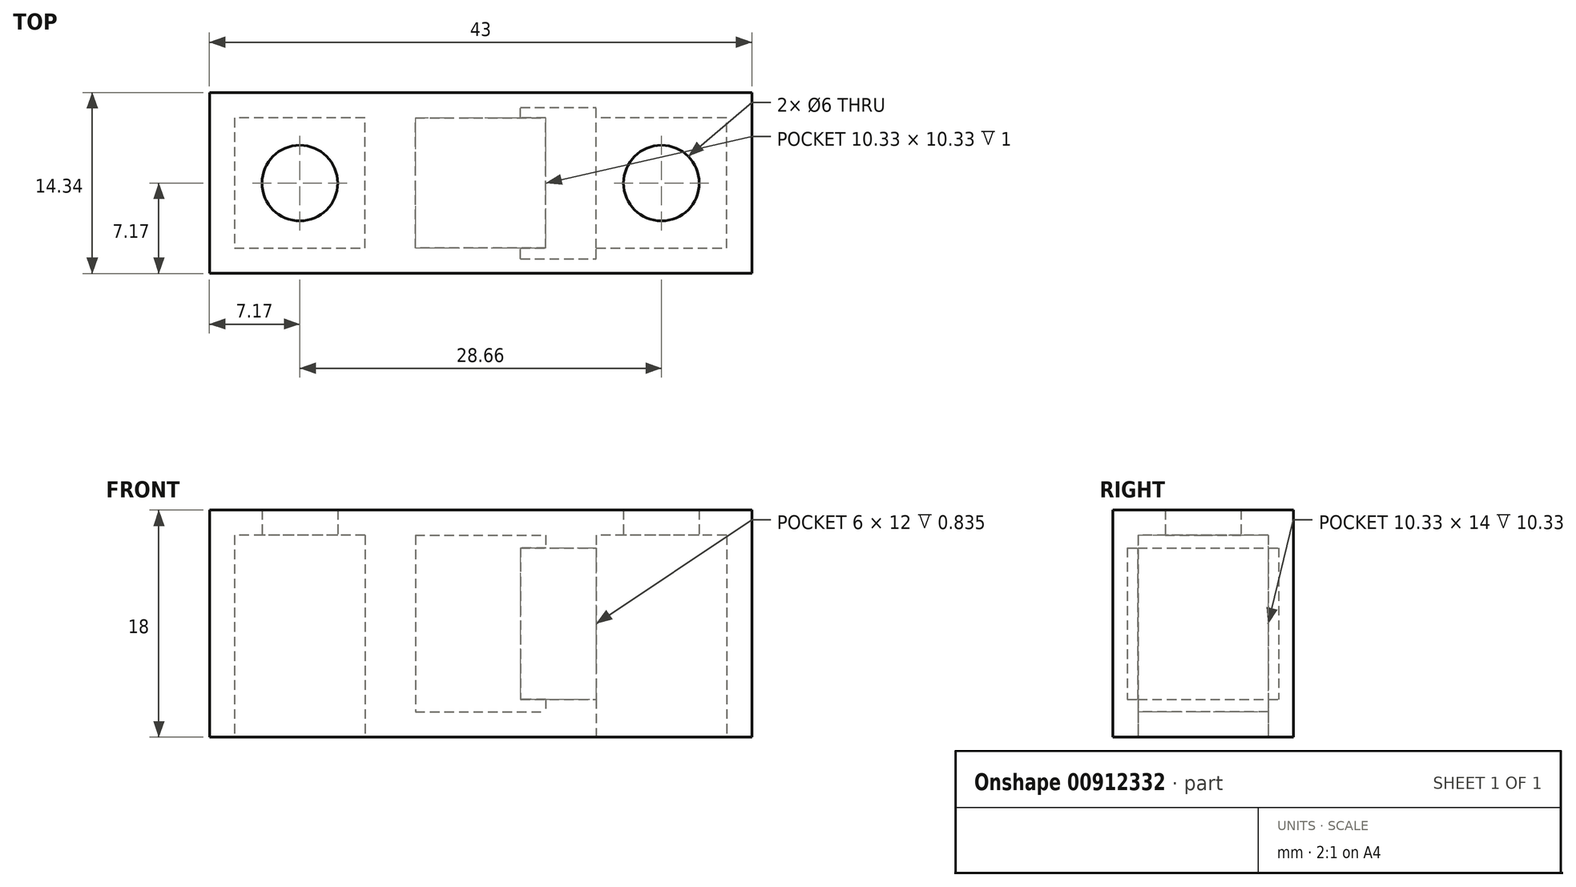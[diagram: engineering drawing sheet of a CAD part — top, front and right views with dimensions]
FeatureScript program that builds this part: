
annotation { "Feature Type Name" : "Feature", "Feature Type Description" : "" }
export const myFeature = defineFeature(function(context is Context, id is Id, definition is map)
    precondition{}
    {
        {
            var Q0;
            Q0=qCreatedBy(makeId("Top.planeOp"),FACE);
            var sketch = newSketch(context, id + "F0", { "sketchPlane" : qUnion([Q0])});
            skLineSegment(sketch, "E0.bottom", {"start": v(-3.17, 3.17) * mm, "end": v(3.16, 3.17) * mm});
            skLineSegment(sketch, "E0.top", {"start": v(-3.17, -3.17) * mm, "end": v(3.17, -3.17) * mm});
            skLineSegment(sketch, "E0.left", {"start": v(-3.17, 3.17) * mm, "end": v(-3.17, -3.17) * mm});
            skLineSegment(sketch, "E0.right", {"start": v(3.17, 3.17) * mm, "end": v(3.17, -3.17) * mm});
            skLineSegment(sketch, "E1", {"start": v(-3.17, 0) * mm, "end": v(3.17, 0) * mm, "construction": true});
            skLineSegment(sketch, "E2", {"start": v(-3.17, 3.17) * mm, "end": v(-5.17, 3.17) * mm, "construction": true});
            skLineSegment(sketch, "E3", {"start": v(-3.17, 3.17) * mm, "end": v(-3.17, 5.17) * mm, "construction": true});
            skLineSegment(sketch, "E4", {"start": v(-5.16, 5.17) * mm, "end": v(5.17, 5.17) * mm});
            skLineSegment(sketch, "E5", {"start": v(5.17, 5.17) * mm, "end": v(5.17, -5.17) * mm});
            skLineSegment(sketch, "E6", {"start": v(5.17, -5.17) * mm, "end": v(-5.16, -5.17) * mm});
            skLineSegment(sketch, "E7", {"start": v(-5.17, -5.16) * mm, "end": v(-5.17, 5.17) * mm});
            skLineSegment(sketch, "E8", {"start": v(3.17, -3.17) * mm, "end": v(3.17, -5.17) * mm, "construction": true});
            skLineSegment(sketch, "E9", {"start": v(-5.17, 3.17) * mm, "end": v(-7.16, 3.17) * mm, "construction": true});
            skLineSegment(sketch, "E10", {"start": v(3.17, -5.17) * mm, "end": v(3.17, -7.16) * mm, "construction": true});
            skLineSegment(sketch, "E11", {"start": v(-3.17, 5.17) * mm, "end": v(-3.17, 7.16) * mm, "construction": true});
            skLineSegment(sketch, "E12", {"start": v(-7.16, 7.16) * mm, "end": v(7.16, 7.16) * mm});
            skLineSegment(sketch, "E13", {"start": v(7.16, 7.16) * mm, "end": v(7.16, -7.16) * mm});
            skLineSegment(sketch, "E14", {"start": v(7.16, -7.16) * mm, "end": v(-7.16, -7.16) * mm});
            skLineSegment(sketch, "E15", {"start": v(-7.16, -7.16) * mm, "end": v(-7.16, 7.16) * mm});
            skLineSegment(sketch, "E16", {"start": v(-7.16, 7.16) * mm, "end": v(-21.5, 7.16) * mm});
            skLineSegment(sketch, "E17", {"start": v(-21.5, 7.16) * mm, "end": v(-21.5, -7.16) * mm});
            skLineSegment(sketch, "E18", {"start": v(-21.5, -7.16) * mm, "end": v(-7.16, -7.16) * mm});
            skLineSegment(sketch, "E19", {"start": v(7.16, 7.16) * mm, "end": v(21.5, 7.16) * mm});
            skLineSegment(sketch, "E20", {"start": v(21.5, 7.16) * mm, "end": v(21.5, -7.16) * mm});
            skLineSegment(sketch, "E21", {"start": v(21.5, -7.16) * mm, "end": v(7.16, -7.16) * mm});
            skLineSegment(sketch, "E22.MirrorCS", {"start": v(-9.16, 5.17) * mm, "end": v(-19.5, 5.17) * mm});
            skLineSegment(sketch, "E23.MirrorCS", {"start": v(-9.16, -5.16) * mm, "end": v(-9.16, 5.16) * mm});
            skLineSegment(sketch, "E24.MirrorCS", {"start": v(-19.5, -5.17) * mm, "end": v(-9.16, -5.17) * mm});
            skLineSegment(sketch, "E25.MirrorCS", {"start": v(-19.5, 5.17) * mm, "end": v(-19.5, -5.16) * mm});
            skLineSegment(sketch, "E26.MirrorCS", {"start": v(9.16, 5.17) * mm, "end": v(9.16, -5.16) * mm});
            skLineSegment(sketch, "E27.MirrorCS", {"start": v(19.5, 5.17) * mm, "end": v(9.16, 5.17) * mm});
            skLineSegment(sketch, "E28.MirrorCS", {"start": v(19.5, -5.16) * mm, "end": v(19.5, 5.17) * mm});
            skLineSegment(sketch, "E29.MirrorCS", {"start": v(9.16, -5.16) * mm, "end": v(19.5, -5.16) * mm});
            skLineSegment(sketch, "E30", {"start": v(-14.33, 5.17) * mm, "end": v(-14.33, -5.17) * mm, "construction": true});
            skLineSegment(sketch, "E31", {"start": v(-19.5, 0) * mm, "end": v(-9.16, 0) * mm, "construction": true});
            skLineSegment(sketch, "E32", {"start": v(0, 3.17) * mm, "end": v(0, -3.17) * mm, "construction": true});
            skLineSegment(sketch, "E33.MirrorCS", {"start": v(14.33, 5.17) * mm, "end": v(14.33, -5.16) * mm, "construction": true});
            skLineSegment(sketch, "E34.MirrorCS", {"start": v(19.5, 0) * mm, "end": v(9.16, 0) * mm, "construction": true});
            skCircle(sketch, "E35", {"center": v(-14.33, 0) * mm, "radius": 3 * mm});
            skCircle(sketch, "E36.MirrorC", {"center": v(14.33, 0) * mm, "radius": 3 * mm});
            skSolve(sketch);
        }
        {
            var Q0;
            Q0=makeQuery(id+"F0.imprint","IMPRINT",FACE,{"disambiguationData":[TD([[makeQuery(id+"F0.imprint","IMPRINT",EDGE,{"derivedFrom":sQuery(id+"F0.wireOp",EDGE,"E15")}),1.0]])]});
            var Q1;
            Q1=makeQuery(id+"F0.imprint","IMPRINT",FACE,{"disambiguationData":[TD([[makeQuery(id+"F0.imprint","IMPRINT",EDGE,{"derivedFrom":sQuery(id+"F0.wireOp",EDGE,"E4")}),1.0]])]});
            var Q2;
            Q2=makeQuery(id+"F0.imprint","IMPRINT",FACE,{"disambiguationData":[TD([[makeQuery(id+"F0.imprint","IMPRINT",EDGE,{"derivedFrom":sQuery(id+"F0.wireOp",EDGE,"E0.bottom")}),1.0]])]});
            var Q3;
            Q3=makeQuery(id+"F0.imprint","IMPRINT",FACE,{"disambiguationData":[TD([[makeQuery(id+"F0.imprint","IMPRINT",EDGE,{"derivedFrom":sQuery(id+"F0.wireOp",EDGE,"E0.bottom")}),-1.0]])]});
            var Q4;
            Q4=makeQuery(id+"F0.imprint","IMPRINT",FACE,{"disambiguationData":[TD([[makeQuery(id+"F0.imprint","IMPRINT",EDGE,{"derivedFrom":sQuery(id+"F0.wireOp",EDGE,"E13")}),1.0]])]});
            extrude(context, id + "F1", {"entities" : qUnion([Q0, Q1, Q2, Q3, Q4]), "depth" : 2 * mm, "offsetDistance" : 25 * mm});
        }
        {
            var Q0;
            Q0=makeQuery(id+"F1.opExtrude","CAP_FACE",FACE,{"disambiguationData":[OSD([sQuery(id+"F0.wireOp",EDGE,"E12"),sQuery(id+"F0.wireOp",EDGE,"E14"),sQuery(id+"F0.wireOp",EDGE,"E16"),sQuery(id+"F0.wireOp",EDGE,"E17"),sQuery(id+"F0.wireOp",EDGE,"E18"),sQuery(id+"F0.wireOp",EDGE,"E19"),sQuery(id+"F0.wireOp",EDGE,"E20"),sQuery(id+"F0.wireOp",EDGE,"E21"),sQuery(id+"F0.wireOp",EDGE,"E22.MirrorCS"),sQuery(id+"F0.wireOp",EDGE,"E23.MirrorCS"),sQuery(id+"F0.wireOp",EDGE,"E24.MirrorCS"),sQuery(id+"F0.wireOp",EDGE,"E25.MirrorCS"),sQuery(id+"F0.wireOp",EDGE,"E26.MirrorCS"),sQuery(id+"F0.wireOp",EDGE,"E27.MirrorCS"),sQuery(id+"F0.wireOp",EDGE,"E28.MirrorCS"),sQuery(id+"F0.wireOp",EDGE,"E29.MirrorCS")])],"isStart":false});
            var sketch = newSketch(context, id + "F2", { "sketchPlane" : qUnion([Q0])});
            skLineSegment(sketch, "E37.0", {"start": v(-9.16, -5.16) * mm, "end": v(-9.16, 5.16) * mm});
            skLineSegment(sketch, "E37.1", {"start": v(-9.16, 5.17) * mm, "end": v(-19.5, 5.17) * mm});
            skLineSegment(sketch, "E37.2", {"start": v(-19.5, 5.17) * mm, "end": v(-19.5, -5.16) * mm});
            skLineSegment(sketch, "E37.3", {"start": v(-19.5, -5.17) * mm, "end": v(-9.16, -5.17) * mm});
            skLineSegment(sketch, "E37.4", {"start": v(-21.5, 7.16) * mm, "end": v(-21.5, -7.16) * mm});
            skLineSegment(sketch, "E37.5", {"start": v(-7.16, 7.16) * mm, "end": v(-21.5, 7.16) * mm});
            skLineSegment(sketch, "E37.6", {"start": v(-7.16, 7.16) * mm, "end": v(7.16, 7.16) * mm});
            skLineSegment(sketch, "E37.7", {"start": v(7.16, 7.16) * mm, "end": v(21.5, 7.16) * mm});
            skLineSegment(sketch, "E37.8", {"start": v(21.5, 7.16) * mm, "end": v(21.5, -7.16) * mm});
            skLineSegment(sketch, "E37.9", {"start": v(21.5, -7.16) * mm, "end": v(7.16, -7.16) * mm});
            skLineSegment(sketch, "E37.10", {"start": v(7.16, -7.16) * mm, "end": v(-7.16, -7.16) * mm});
            skLineSegment(sketch, "E37.11", {"start": v(-21.5, -7.16) * mm, "end": v(-7.16, -7.16) * mm});
            skLineSegment(sketch, "E37.12", {"start": v(-5.17, -5.16) * mm, "end": v(-5.17, 5.17) * mm});
            skLineSegment(sketch, "E37.13", {"start": v(-5.16, 5.17) * mm, "end": v(5.17, 5.17) * mm});
            skLineSegment(sketch, "E37.14", {"start": v(5.17, 5.17) * mm, "end": v(5.17, -5.17) * mm});
            skLineSegment(sketch, "E37.15", {"start": v(5.17, -5.17) * mm, "end": v(-5.16, -5.17) * mm});
            skLineSegment(sketch, "E37.16", {"start": v(9.16, 5.17) * mm, "end": v(9.16, -5.16) * mm});
            skLineSegment(sketch, "E37.17", {"start": v(19.5, 5.17) * mm, "end": v(9.16, 5.17) * mm});
            skLineSegment(sketch, "E37.18", {"start": v(19.5, -5.16) * mm, "end": v(19.5, 5.17) * mm});
            skLineSegment(sketch, "E37.19", {"start": v(9.16, -5.16) * mm, "end": v(19.5, -5.16) * mm});
            skSolve(sketch);
        }
        {
            var Q0;
            Q0=makeQuery(id+"F2.imprint","IMPRINT",FACE,{"disambiguationData":[TD([[makeQuery(id+"F2.imprint","IMPRINT",EDGE,{"derivedFrom":sQuery(id+"F2.wireOp",EDGE,"E37.0")}),-1.0]])]});
            extrude(context, id + "F3", {"entities" : qUnion([Q0]), "operationType" : NewBodyOperationType.ADD, "depth" : 14 * mm, "offsetDistance" : 25 * mm});
        }
        {
            var Q0;
            Q0=makeQuery(id+"F3.opExtrude","CAP_FACE",FACE,{"disambiguationData":[OSD([sQuery(id+"F2.wireOp",EDGE,"E37.0"),sQuery(id+"F2.wireOp",EDGE,"E37.1"),sQuery(id+"F2.wireOp",EDGE,"E37.2"),sQuery(id+"F2.wireOp",EDGE,"E37.3"),sQuery(id+"F2.wireOp",EDGE,"E37.4"),sQuery(id+"F2.wireOp",EDGE,"E37.5"),sQuery(id+"F2.wireOp",EDGE,"E37.6"),sQuery(id+"F2.wireOp",EDGE,"E37.7"),sQuery(id+"F2.wireOp",EDGE,"E37.8"),sQuery(id+"F2.wireOp",EDGE,"E37.9"),sQuery(id+"F2.wireOp",EDGE,"E37.10"),sQuery(id+"F2.wireOp",EDGE,"E37.11"),sQuery(id+"F2.wireOp",EDGE,"E37.12"),sQuery(id+"F2.wireOp",EDGE,"E37.13"),sQuery(id+"F2.wireOp",EDGE,"E37.14"),sQuery(id+"F2.wireOp",EDGE,"E37.15"),sQuery(id+"F2.wireOp",EDGE,"E37.16"),sQuery(id+"F2.wireOp",EDGE,"E37.17"),sQuery(id+"F2.wireOp",EDGE,"E37.18"),sQuery(id+"F2.wireOp",EDGE,"E37.19")])],"isStart":false});
            var sketch = newSketch(context, id + "F4", { "sketchPlane" : qUnion([Q0])});
            skCircle(sketch, "E38.0", {"center": v(-14.33, 0) * mm, "radius": 3 * mm});
            skCircle(sketch, "E38.1", {"center": v(14.33, 0) * mm, "radius": 3 * mm});
            skLineSegment(sketch, "E38.2", {"start": v(7.16, 7.16) * mm, "end": v(21.5, 7.16) * mm});
            skLineSegment(sketch, "E38.3", {"start": v(21.5, 7.16) * mm, "end": v(21.5, -7.16) * mm});
            skLineSegment(sketch, "E38.4", {"start": v(21.5, -7.16) * mm, "end": v(7.16, -7.16) * mm});
            skLineSegment(sketch, "E38.5", {"start": v(7.16, -7.16) * mm, "end": v(-7.16, -7.16) * mm});
            skLineSegment(sketch, "E38.6", {"start": v(-21.5, -7.16) * mm, "end": v(-7.16, -7.16) * mm});
            skLineSegment(sketch, "E38.7", {"start": v(-21.5, 7.16) * mm, "end": v(-21.5, -7.16) * mm});
            skLineSegment(sketch, "E38.8", {"start": v(-7.16, 7.16) * mm, "end": v(-21.5, 7.16) * mm});
            skLineSegment(sketch, "E38.9", {"start": v(-7.16, 7.16) * mm, "end": v(7.16, 7.16) * mm});
            skSolve(sketch);
        }
        {
            var Q0;
            Q0 = qSketchRegion(id + "F4", true);
            extrude(context, id + "F5", {"entities" : qUnion([Q0]), "operationType" : NewBodyOperationType.ADD, "depth" : 2 * mm, "offsetDistance" : 25 * mm});
        }
        {
            var Q0;
            Q0=makeQuery(id+"F3.boolean.opBoolean","MERGE",FACE,{"derivedFrom":[makeQuery(id+"F1.opExtrude","SWEPT_FACE",FACE,{"disambiguationData":[OSD([sQuery(id+"F0.wireOp",EDGE,"E26.MirrorCS")])]}),makeQuery(id+"F3.opExtrude","SWEPT_FACE",FACE,{"disambiguationData":[OSD([sQuery(id+"F2.wireOp",EDGE,"E37.16")])]})]});
            var sketch = newSketch(context, id + "F6", { "sketchPlane" : qUnion([Q0])});
            skLineSegment(sketch, "E39", {"start": v(0, 0) * mm, "end": v(0, 3) * mm, "construction": true});
            skLineSegment(sketch, "E40.bottom", {"start": v(-6, 15) * mm, "end": v(6, 15) * mm});
            skLineSegment(sketch, "E40.top", {"start": v(-6, 3) * mm, "end": v(6, 3) * mm});
            skLineSegment(sketch, "E40.left", {"start": v(-6, 15) * mm, "end": v(-6, 3) * mm});
            skLineSegment(sketch, "E40.right", {"start": v(6, 15) * mm, "end": v(6, 3) * mm});
            skSolve(sketch);
        }
        {
            var Q0;
            Q0=makeQuery(id+"F6.imprint","IMPRINT",FACE,{"disambiguationData":[TD([[makeQuery(id+"F6.imprint","IMPRINT",EDGE,{"derivedFrom":sQuery(id+"F6.wireOp",EDGE,"E40.bottom")}),-1.0]])]});
            extrude(context, id + "F7", {"entities" : qUnion([Q0]), "operationType" : NewBodyOperationType.REMOVE, "oppositeDirection" : true, "depth" : 6 * mm, "offsetDistance" : 25 * mm});
        }
    });
